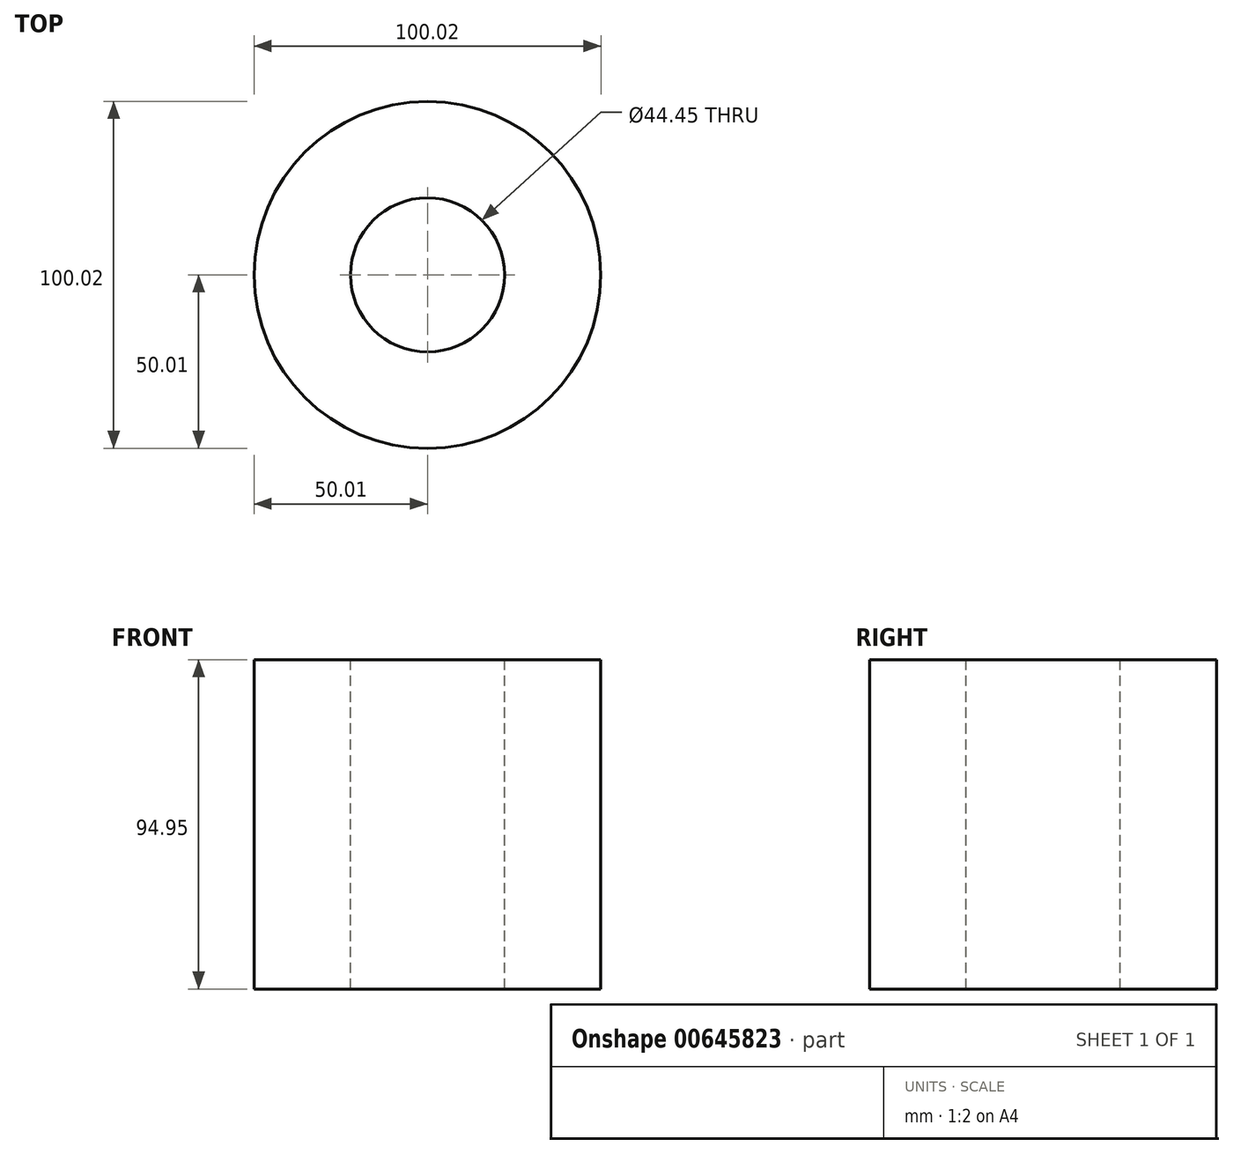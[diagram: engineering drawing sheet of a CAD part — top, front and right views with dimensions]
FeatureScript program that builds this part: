
annotation { "Feature Type Name" : "Feature", "Feature Type Description" : "" }
export const myFeature = defineFeature(function(context is Context, id is Id, definition is map)
    precondition{}
    {
        {
            var Q0;
            Q0=qCreatedBy(makeId("Top.planeOp"),FACE);
            var sketch = newSketch(context, id + "F0", { "sketchPlane" : qUnion([Q0])});
            skCircle(sketch, "E0", {"center": v(0, 0) * mm, "radius": 50 * mm});
            skSolve(sketch);
        }
        {
            var Q0;
            Q0 = qSketchRegion(id + "F0", true);
            extrude(context, id + "F1", {"entities" : qUnion([Q0]), "depth" : 94.95 * mm, "offsetDistance" : 25.4 * mm});
        }
        {
            var Q0;
            Q0=makeQuery(id+"F1.opExtrude","CAP_FACE",FACE,{"disambiguationData":[OSD([sQuery(id+"F0.wireOp",EDGE,"E0")])],"isStart":false});
            var sketch = newSketch(context, id + "F2", { "sketchPlane" : qUnion([Q0])});
            skCircle(sketch, "E1", {"center": v(0, 0) * mm, "radius": 22.23 * mm});
            skSolve(sketch);
        }
        {
            var Q0;
            Q0=makeQuery(id+"F2.imprint","IMPRINT",FACE,{"disambiguationData":[TD([[makeQuery(id+"F2.imprint","IMPRINT",EDGE,{"derivedFrom":sQuery(id+"F2.wireOp",EDGE,"E1")}),1.0]])]});
            extrude(context, id + "F3", {"entities" : qUnion([Q0]), "operationType" : NewBodyOperationType.REMOVE, "endBound" : BoundingType.THROUGH_ALL, "oppositeDirection" : true, "depth" : 25.4 * mm, "offsetDistance" : 25.4 * mm});
        }
    });
